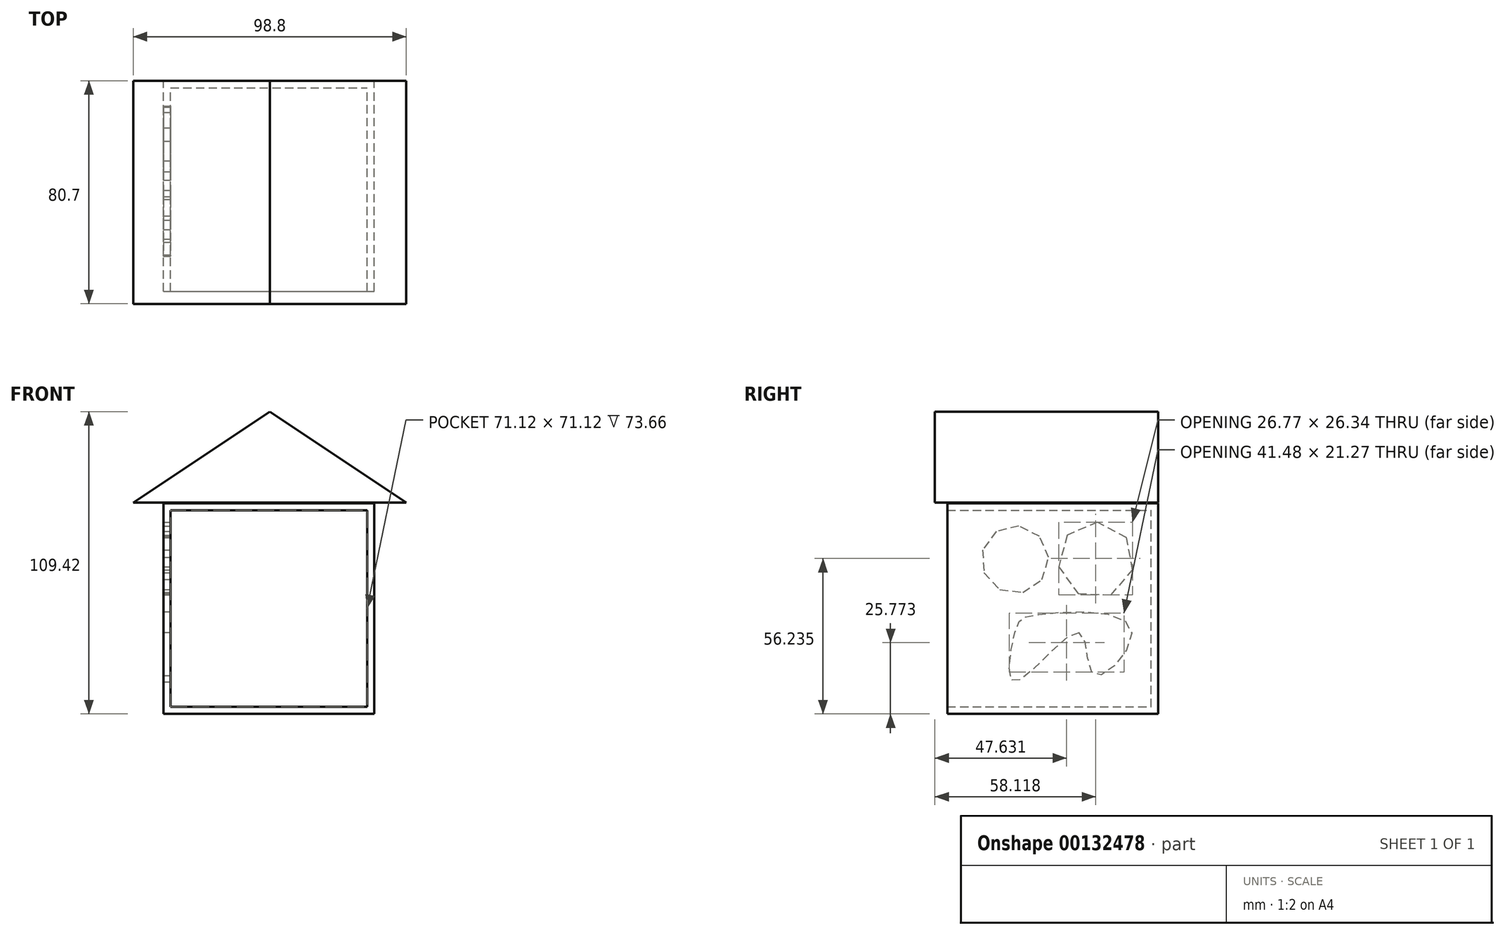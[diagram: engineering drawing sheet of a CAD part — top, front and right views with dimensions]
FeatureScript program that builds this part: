
annotation { "Feature Type Name" : "Feature", "Feature Type Description" : "" }
export const myFeature = defineFeature(function(context is Context, id is Id, definition is map)
    precondition{}
    {
        {
            var Q0;
            Q0=qCreatedBy(makeId("Front.planeOp"),FACE);
            var sketch = newSketch(context, id + "F0", { "sketchPlane" : qUnion([Q0])});
            skLineSegment(sketch, "E0.bottom", {"start": v(-38.1, -38.1) * mm, "end": v(38.1, -38.1) * mm});
            skLineSegment(sketch, "E0.top", {"start": v(-38.1, 38.1) * mm, "end": v(38.1, 38.1) * mm});
            skLineSegment(sketch, "E0.left", {"start": v(-38.1, -38.1) * mm, "end": v(-38.1, 38.1) * mm});
            skLineSegment(sketch, "E0.right", {"start": v(38.1, -38.1) * mm, "end": v(38.1, 38.1) * mm});
            skPoint(sketch, "E0.middle", {"position": v(0, 0) * mm});
            skSolve(sketch);
        }
        {
            var Q0;
            Q0=makeQuery(id+"F0.imprint","IMPRINT",FACE,{"disambiguationData":[TD([[makeQuery(id+"F0.imprint","IMPRINT",EDGE,{"derivedFrom":sQuery(id+"F0.wireOp",EDGE,"E0.bottom")}),1.0]])]});
            extrude(context, id + "F1", {"entities" : qUnion([Q0]), "depth" : 76.2 * mm});
        }
        {
            var Q0;
            Q0=makeQuery(id+"F1.opExtrude","CAP_FACE",FACE,{"disambiguationData":[OSD([sQuery(id+"F0.wireOp",EDGE,"E0.bottom"),sQuery(id+"F0.wireOp",EDGE,"E0.top"),sQuery(id+"F0.wireOp",EDGE,"E0.left"),sQuery(id+"F0.wireOp",EDGE,"E0.right")])],"isStart":false});
            shell(context, id + "F2", {"entities" : qUnion([Q0]), "thickness" : 2.54 * mm});
        }
        {
            var Q0;
            Q0=qCreatedBy(makeId("Front.planeOp"),FACE);
            var sketch = newSketch(context, id + "F3", { "sketchPlane" : qUnion([Q0])});
            skLineSegment(sketch, "E1", {"start": v(49.7, 38.39) * mm, "end": v(-49.1, 38.39) * mm});
            skLineSegment(sketch, "E2", {"start": v(-49.1, 38.39) * mm, "end": v(0.4, 71.32) * mm});
            skLineSegment(sketch, "E3", {"start": v(0.4, 71.32) * mm, "end": v(49.7, 38.39) * mm});
            skSolve(sketch);
        }
        {
            var Q0;
            Q0=makeQuery(id+"F3.imprint","IMPRINT",FACE,{"disambiguationData":[TD([[makeQuery(id+"F3.imprint","IMPRINT",EDGE,{"derivedFrom":sQuery(id+"F3.wireOp",EDGE,"E1")}),-1.0]])]});
            extrude(context, id + "F4", {"entities" : qUnion([Q0]), "depth" : 80.7 * mm});
        }
        {
            var Q0;
            Q0=qCreatedBy(makeId("Right.planeOp"),FACE);
            var sketch = newSketch(context, id + "F5", { "sketchPlane" : qUnion([Q0])});
            skCircle(sketch, "E4.cCircle", {"center": v(-22.46, 17.58) * mm, "radius": 13.74 * mm, "construction": true});
            skLineSegment(sketch, "E4.0", {"start": v(-28.92, 5.46) * mm, "end": v(-35.96, 15.07) * mm});
            skLineSegment(sketch, "E4.1", {"start": v(-35.96, 15.07) * mm, "end": v(-32.84, 26.58) * mm});
            skLineSegment(sketch, "E4.2", {"start": v(-32.84, 26.58) * mm, "end": v(-21.9, 31.3) * mm});
            skLineSegment(sketch, "E4.3", {"start": v(-21.9, 31.3) * mm, "end": v(-11.37, 25.7) * mm});
            skLineSegment(sketch, "E4.4", {"start": v(-11.37, 25.7) * mm, "end": v(-9.2, 13.97) * mm});
            skLineSegment(sketch, "E4.5", {"start": v(-9.2, 13.97) * mm, "end": v(-17, 4.96) * mm});
            skLineSegment(sketch, "E4.6", {"start": v(-17, 4.96) * mm, "end": v(-28.92, 5.46) * mm});
            skFitSpline(sketch, "E5", {"points": [v(-28.52, -8.69) * mm, v(-51.95, -26.47) * mm, v(-51.35, -7.27) * mm, v(-45.29, -2.42) * mm, v(-9.73, -7.27) * mm, v(-22.86, -24.04) * mm, v(-28.52, -8.69) * mm]});
            skCircle(sketch, "E6.cCircle", {"center": v(-51.75, 17.78) * mm, "radius": 12.2 * mm, "construction": true});
            skLineSegment(sketch, "E6.0", {"start": v(-57.2, 6.87) * mm, "end": v(-62.94, 12.93) * mm});
            skLineSegment(sketch, "E6.1", {"start": v(-62.94, 12.93) * mm, "end": v(-63.44, 21.26) * mm});
            skLineSegment(sketch, "E6.2", {"start": v(-63.44, 21.26) * mm, "end": v(-58.47, 27.96) * mm});
            skLineSegment(sketch, "E6.3", {"start": v(-58.47, 27.96) * mm, "end": v(-50.36, 29.9) * mm});
            skLineSegment(sketch, "E6.4", {"start": v(-50.36, 29.9) * mm, "end": v(-42.9, 26.17) * mm});
            skLineSegment(sketch, "E6.5", {"start": v(-42.9, 26.17) * mm, "end": v(-39.58, 18.51) * mm});
            skLineSegment(sketch, "E6.6", {"start": v(-39.58, 18.51) * mm, "end": v(-41.96, 10.51) * mm});
            skLineSegment(sketch, "E6.7", {"start": v(-41.96, 10.51) * mm, "end": v(-48.92, 5.92) * mm});
            skLineSegment(sketch, "E6.8", {"start": v(-48.92, 5.92) * mm, "end": v(-57.2, 6.87) * mm});
            skSolve(sketch);
        }
        {
            var Q0;
            Q0=makeQuery(id+"F5.imprint","IMPRINT",FACE,{"disambiguationData":[TD([[makeQuery(id+"F5.imprint","IMPRINT",EDGE,{"derivedFrom":sQuery(id+"F5.wireOp",EDGE,"E6.0")}),-1.0]])]});
            extrude(context, id + "F6", {"entities" : qUnion([Q0]), "operationType" : NewBodyOperationType.REMOVE, "oppositeDirection" : true, "depth" : 72.35 * mm});
        }
        {
            var Q0;
            Q0 = qSketchRegion(id + "F5", true);
            extrude(context, id + "F7", {"entities" : qUnion([Q0]), "operationType" : NewBodyOperationType.REMOVE, "oppositeDirection" : true, "depth" : 45.28 * mm});
        }
    });
